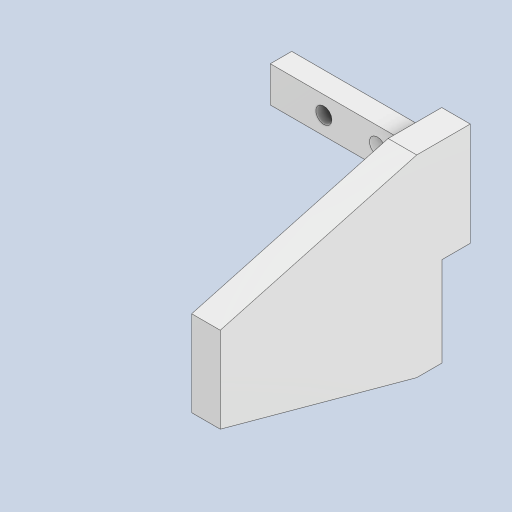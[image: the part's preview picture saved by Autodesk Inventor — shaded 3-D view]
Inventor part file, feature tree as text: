
AUTODESK INVENTOR PART (.ipt)
format: ipt  version: 2023 (Build 270158000, 158)  size: 137,728 bytes
history: native  units: in
note: dims shown in document units (in); Inventor stores cm internally (conversion verified against a paired STEP export)
features: extrude x4, sketch x3
ambient origin geometry x8: Origin, YZ Plane, XZ Plane, XY Plane, X Axis, Y Axis, Z Axis, Center Point
bodies: Body1 (feature_tree)
feature tree (7):
  sketch  "スケッチ2"
  extrude  "押し出し2"  Depth=1.9685in
  extrude  "押し出し5"  Depth=0.3937in
  extrude  "押し出し6"  Depth=0.315in
  extrude  "押し出し7"  Depth=0.1772in
  sketch  "スケッチ4"
  sketch  "スケッチ5"
